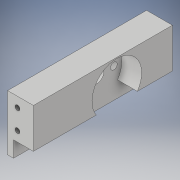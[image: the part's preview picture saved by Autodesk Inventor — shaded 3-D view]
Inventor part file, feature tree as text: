
AUTODESK INVENTOR PART (.ipt)
format: ipt  version: 2019 (Build 230136000, 136)  size: 176,640 bytes
history: native  units: in
note: dims shown in document units (in); Inventor stores cm internally (conversion verified against a paired STEP export)
features: extrude x4, sketch x4, hole x3
ambient origin geometry x8: Origin, YZ Plane, XZ Plane, XY Plane, X Axis, Y Axis, Z Axis, Center Point
bodies: Solid1 (feature_tree)
feature tree (11):
  extrude  "Extrusion1"  Depth=0.3937in TaperAngle=0.0deg
  extrude  "Extrusion2"  Depth=0.1181in TaperAngle=0.0deg
  extrude  "Extrusion3"  Depth=1.1024in
  extrude  "Extrusion4"  Depth=0.3937in
  hole  "Hole1"  [1 undecoded]
  hole  "Hole2"  [1 undecoded]
  hole  "Hole4"  [1 undecoded]
  sketch  "Sketch3"  dims[d2=0.5118in d3=0.0in d6=0.3937in d7=0.0in]
  sketch  "Sketch5"  dims[d11=0.3937in d12=0.0in d18=0.1181in d19=0.0in]
  sketch  "Sketch6"  dims[d20=2.7559in d21=1.1024in]
  sketch  "Sketch9"  dims[d22=0.5906in d23=0.9843in d24=0.2756in d25=0.3346in d26=0.3346in d29=0.1969in d30=0.1969in d31=0.1969in d32=0.1969in d33=0.097in d34=0.3937in d35=0.248in d36=0.25in d37=90.0deg d38=0.3937in d39=0.8108in d40=0.097in d41=0.3937in d42=0.248in d43=0.25in d44=90.0deg d45=0.3937in d46=0.8108in d60=0.163in d61=0.3937in d62=0.433in d63=0.102in d64=90.0deg d65=0.3937in d66=0.8108in d68=0.1339in d69=0.1339in d70=0.1969in d71=0.5906in d74=0.1969in d75=0.4724in d47=0.75in d48=0.8108in d49=0.0625in d50=0.75in d51=0.375in]
note: 3 required parameter values undecoded (feature->parameter linkage not recoverable at this tier; creation-order binding heuristic only, values carry confidence <= 0.55)
